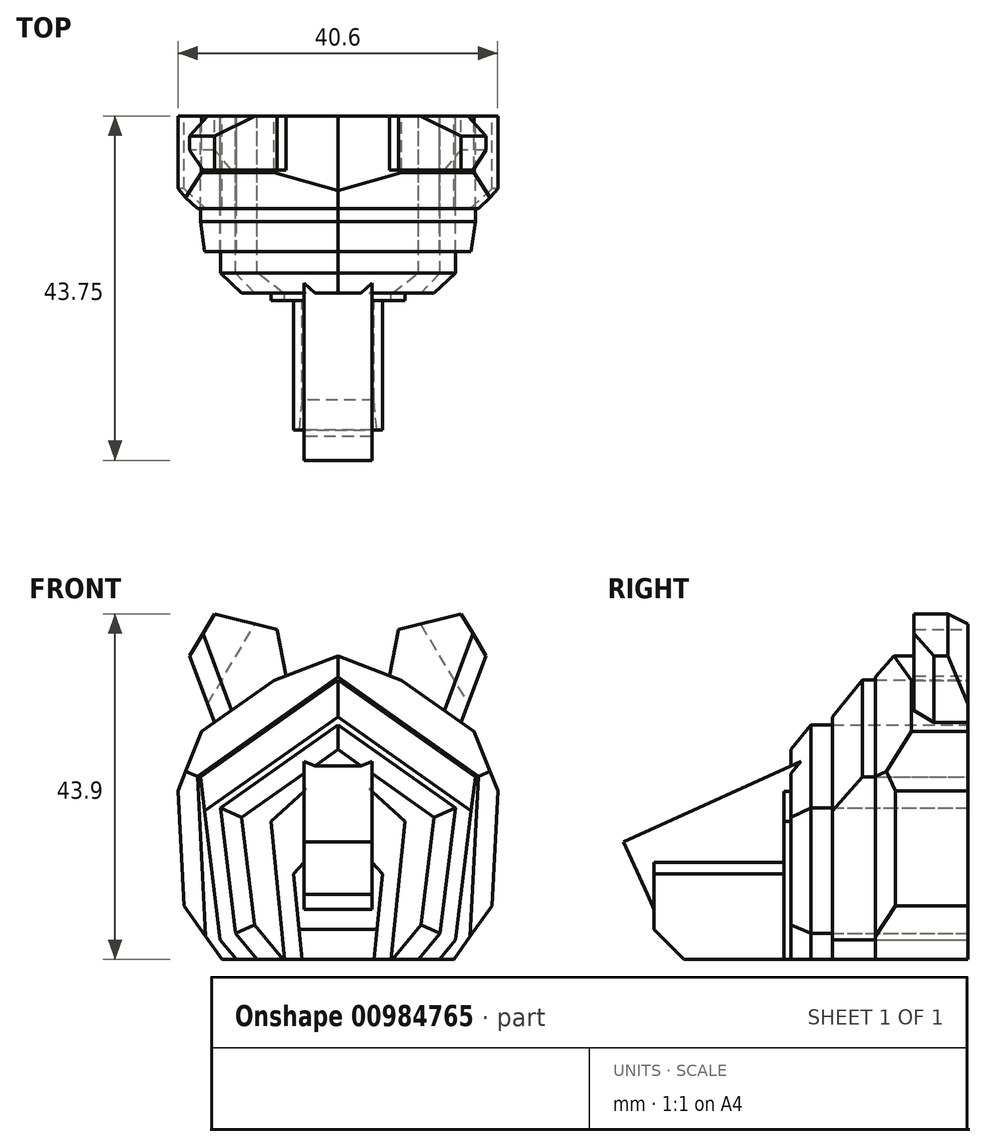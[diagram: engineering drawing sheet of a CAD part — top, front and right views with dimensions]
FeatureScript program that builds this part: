
annotation { "Feature Type Name" : "Feature", "Feature Type Description" : "" }
export const myFeature = defineFeature(function(context is Context, id is Id, definition is map)
    precondition{}
    {
        {
            var Q0;
            Q0=qCreatedBy(makeId("Front.planeOp"),FACE);
            var sketch = newSketch(context, id + "F0", { "sketchPlane" : qUnion([Q0])});
            skLineSegment(sketch, "E0", {"start": v(0, 23) * mm, "end": v(-2.53, 23) * mm});
            skLineSegment(sketch, "E1", {"start": v(-2.53, 23) * mm, "end": v(-8.52, 17.52) * mm});
            skLineSegment(sketch, "E2", {"start": v(-8.52, 17.52) * mm, "end": v(-6.77, 0) * mm});
            skLineSegment(sketch, "E3.MirrorCS", {"start": v(0, 23) * mm, "end": v(2.53, 23) * mm});
            skLineSegment(sketch, "E4.MirrorCS", {"start": v(2.53, 23) * mm, "end": v(8.52, 17.52) * mm});
            skLineSegment(sketch, "E5.MirrorCS", {"start": v(8.52, 17.52) * mm, "end": v(6.77, 0) * mm});
            skLineSegment(sketch, "E6", {"start": v(2.53, 14.3) * mm, "end": v(5.66, 10.9) * mm});
            skLineSegment(sketch, "E7", {"start": v(5.66, 10.9) * mm, "end": v(4.57, 0) * mm});
            skLineSegment(sketch, "E8", {"start": v(2.53, 14.3) * mm, "end": v(0, 14.3) * mm});
            skLineSegment(sketch, "E9.MirrorCS", {"start": v(-2.53, 14.3) * mm, "end": v(0, 14.3) * mm});
            skLineSegment(sketch, "E10.MirrorCS", {"start": v(-2.53, 14.3) * mm, "end": v(-5.66, 10.9) * mm});
            skLineSegment(sketch, "E11.MirrorCS", {"start": v(-5.66, 10.9) * mm, "end": v(-4.57, 0) * mm});
            skLineSegment(sketch, "E12", {"start": v(0, 29.78) * mm, "end": v(-14.93, 19.24) * mm});
            skLineSegment(sketch, "E13", {"start": v(-14.93, 19.24) * mm, "end": v(-13, 3.32) * mm});
            skLineSegment(sketch, "E14", {"start": v(-13, 3.32) * mm, "end": v(-10.24, 0) * mm});
            skLineSegment(sketch, "E15.MirrorCS", {"start": v(0, 29.78) * mm, "end": v(14.93, 19.24) * mm});
            skLineSegment(sketch, "E16.MirrorCS", {"start": v(14.93, 19.24) * mm, "end": v(13, 3.32) * mm});
            skLineSegment(sketch, "E17.MirrorCS", {"start": v(13, 3.32) * mm, "end": v(10.24, 0) * mm});
            skLineSegment(sketch, "E18", {"start": v(0, 38.59) * mm, "end": v(-8.09, 35.46) * mm});
            skLineSegment(sketch, "E19", {"start": v(-8.09, 35.46) * mm, "end": v(-17.3, 28.95) * mm});
            skLineSegment(sketch, "E20", {"start": v(-17.3, 28.95) * mm, "end": v(-20.3, 21.44) * mm});
            skLineSegment(sketch, "E21", {"start": v(-20.3, 21.44) * mm, "end": v(-19.55, 6.83) * mm});
            skLineSegment(sketch, "E22", {"start": v(-19.55, 6.83) * mm, "end": v(-14.72, 0) * mm});
            skLineSegment(sketch, "E23.MirrorCS", {"start": v(0, 38.59) * mm, "end": v(8.09, 35.46) * mm});
            skLineSegment(sketch, "E24.MirrorCS", {"start": v(17.3, 28.95) * mm, "end": v(20.3, 21.44) * mm});
            skLineSegment(sketch, "E25.MirrorCS", {"start": v(8.09, 35.46) * mm, "end": v(17.3, 28.95) * mm});
            skLineSegment(sketch, "E26.MirrorCS", {"start": v(20.3, 21.44) * mm, "end": v(19.55, 6.83) * mm});
            skLineSegment(sketch, "E27.MirrorCS", {"start": v(19.55, 6.83) * mm, "end": v(14.72, 0) * mm});
            skLineSegment(sketch, "E28", {"start": v(-14.72, 0) * mm, "end": v(14.72, 0) * mm});
            skLineSegment(sketch, "E29", {"start": v(6.58, 36.04) * mm, "end": v(7.72, 41.9) * mm});
            skLineSegment(sketch, "E30", {"start": v(7.72, 41.9) * mm, "end": v(15.66, 43.9) * mm});
            skLineSegment(sketch, "E31", {"start": v(15.66, 43.9) * mm, "end": v(18.82, 38.59) * mm});
            skPoint(sketch, "E32.endSnap0", {"position": v(12.7, 32.2) * mm});
            skLineSegment(sketch, "E33", {"start": v(18.82, 38.59) * mm, "end": v(15.66, 30.1) * mm});
            skLineSegment(sketch, "E34.MirrorCS", {"start": v(-6.58, 36.04) * mm, "end": v(-7.72, 41.9) * mm});
            skLineSegment(sketch, "E35.MirrorCS", {"start": v(-7.72, 41.9) * mm, "end": v(-15.66, 43.9) * mm});
            skLineSegment(sketch, "E36.MirrorCS", {"start": v(-15.66, 43.9) * mm, "end": v(-18.82, 38.59) * mm});
            skLineSegment(sketch, "E37.MirrorCS", {"start": v(-18.82, 38.59) * mm, "end": v(-15.66, 30.1) * mm});
            skLineSegment(sketch, "E38", {"start": v(0, 35.5) * mm, "end": v(-17.46, 23.17) * mm});
            skLineSegment(sketch, "E39", {"start": v(-17.46, 23.17) * mm, "end": v(-14.95, 2.47) * mm});
            skLineSegment(sketch, "E40", {"start": v(-14.95, 2.47) * mm, "end": v(-12.9, 0) * mm});
            skLineSegment(sketch, "E41.MirrorCS", {"start": v(0, 35.5) * mm, "end": v(17.46, 23.17) * mm});
            skLineSegment(sketch, "E42.MirrorCS", {"start": v(17.46, 23.17) * mm, "end": v(14.95, 2.47) * mm});
            skLineSegment(sketch, "E43.MirrorCS", {"start": v(14.95, 2.47) * mm, "end": v(12.9, 0) * mm});
            skSolve(sketch);
        }
        {
            var Q0;
            Q0=qCreatedBy(makeId("Right.planeOp"),FACE);
            var sketch = newSketch(context, id + "F1", { "sketchPlane" : qUnion([Q0])});
            skLineSegment(sketch, "E44", {"start": v(0, 38.33) * mm, "end": v(-11.79, 36.33) * mm});
            skLineSegment(sketch, "E45", {"start": v(-11.79, 36.33) * mm, "end": v(-21.78, 29.2) * mm});
            skLineSegment(sketch, "E46", {"start": v(-21.78, 29.2) * mm, "end": v(-24.49, 0) * mm});
            skLineSegment(sketch, "E47", {"start": v(-22.2, 24.73) * mm, "end": v(-43.75, 14.95) * mm});
            skLineSegment(sketch, "E48", {"start": v(-43.75, 14.95) * mm, "end": v(-40.72, 8.26) * mm});
            skLineSegment(sketch, "E49", {"start": v(-22.78, 18.43) * mm, "end": v(-39.87, 13.75) * mm});
            skLineSegment(sketch, "E50", {"start": v(-39.87, 13.75) * mm, "end": v(-40.72, 8.26) * mm});
            skLineSegment(sketch, "E51", {"start": v(-40.72, 8.26) * mm, "end": v(-37.52, 1.02) * mm});
            skLineSegment(sketch, "E52", {"start": v(-37.52, 1.02) * mm, "end": v(-24.49, 0) * mm});
            skLineSegment(sketch, "E53", {"start": v(-24.49, 0) * mm, "end": v(0, 0) * mm});
            skLineSegment(sketch, "E54", {"start": v(0, 38.33) * mm, "end": v(0, 0) * mm});
            skLineSegment(sketch, "E55", {"start": v(-21.78, 29.2) * mm, "end": v(-21.78, 0) * mm});
            skLineSegment(sketch, "E56", {"start": v(-11.79, 36.33) * mm, "end": v(-11.79, 0) * mm});
            skPoint(sketch, "E56.endSnap0", {"position": v(-12.24, 0) * mm});
            skLineSegment(sketch, "E57", {"start": v(-21.78, 15.58) * mm, "end": v(-11.79, 15.58) * mm});
            skSolve(sketch);
        }
        {
            var Q0;
            Q0=makeQuery(id+"F0.imprint","IMPRINT",FACE,{"disambiguationData":[TD([[makeQuery(id+"F0.imprint","IMPRINT",EDGE,{"derivedFrom":sQuery(id+"F0.wireOp",EDGE,"E6")}),-1.0]])]});
            var Q1;
            Q1=sQuery(id+"F1.wireOp",VERTEX,"E49.end");
            extrude(context, id + "F2", {"entities" : qUnion([Q0]), "endBound" : BoundingType.UP_TO_VERTEX, "depth" : 25.4 * mm, "endBoundEntityVertex" : qUnion([Q1]), "offsetDistance" : 25.4 * mm});
        }
        {
            var Q0;
            Q0=makeQuery(id+"F0.imprint","IMPRINT",FACE,{"disambiguationData":[TD([[makeQuery(id+"F0.imprint","IMPRINT",EDGE,{"derivedFrom":sQuery(id+"F0.wireOp",EDGE,"E0")}),1.0]])]});
            extrude(context, id + "F3", {"entities" : qUnion([Q0]), "operationType" : NewBodyOperationType.ADD, "depth" : 23.42 * mm, "offsetDistance" : 25.4 * mm});
        }
        {
            var Q0;
            {var subQ0=sQuery(id+"F1.wireOp",EDGE,"E49");Q0=makeQuery(id+"F1.imprint","IMPRINT",FACE,{"disambiguationData":[TD([[makeQuery(id+"F1.imprint","IMPRINT",EDGE,{"derivedFrom":subQ0}),1.0]])]});}
            var Q1;
            Q1=makeQuery(id+"F3.opExtrude","CAP_VERTEX",VERTEX,{"disambiguationData":[OSD([sQuery(id+"F0.wireOp",EDGE,"E6"),sQuery(id+"F0.wireOp",EDGE,"E8"),sQuery(id+"F0.wireOp",EDGE,"E9.MirrorCS")])],"isStart":false});
            extrude(context, id + "F4", {"entities" : qUnion([Q0]), "operationType" : NewBodyOperationType.ADD, "endBound" : BoundingType.UP_TO_VERTEX, "depth" : 25.4 * mm, "endBoundEntityVertex" : qUnion([Q1]), "offsetDistance" : 25.4 * mm});
        }
        {
            var Q0;
            {var subQ0=sQuery(id+"F1.wireOp",EDGE,"E49");Q0=makeQuery(id+"F1.imprint","IMPRINT",FACE,{"disambiguationData":[TD([[makeQuery(id+"F1.imprint","IMPRINT",EDGE,{"derivedFrom":subQ0}),1.0]])]});}
            var Q1;
            Q1=makeQuery(id+"F3.opExtrude","CAP_VERTEX",VERTEX,{"disambiguationData":[OSD([sQuery(id+"F0.wireOp",EDGE,"E8"),sQuery(id+"F0.wireOp",EDGE,"E9.MirrorCS"),sQuery(id+"F0.wireOp",EDGE,"E10.MirrorCS")])],"isStart":false});
            extrude(context, id + "F5", {"entities" : qUnion([Q0]), "operationType" : NewBodyOperationType.ADD, "endBound" : BoundingType.UP_TO_VERTEX, "oppositeDirection" : true, "depth" : 25.4 * mm, "endBoundEntityVertex" : qUnion([Q1]), "offsetDistance" : 25.4 * mm});
        }
        {
            var Q0;
            {var subQ1=sQuery(id+"F1.wireOp",EDGE,"E47");Q0=makeQuery(id+"F1.imprint","IMPRINT",FACE,{"disambiguationData":[TD([[makeQuery(id+"F1.imprint","IMPRINT",EDGE,{"derivedFrom":subQ1}),1.0]])]});}
            var Q1;
            Q1=makeQuery(id+"F2.opExtrude","CAP_VERTEX",VERTEX,{"disambiguationData":[OSD([sQuery(id+"F0.wireOp",EDGE,"E6"),sQuery(id+"F0.wireOp",EDGE,"E8"),sQuery(id+"F0.wireOp",EDGE,"E9.MirrorCS")])],"isStart":false});
            extrude(context, id + "F6", {"entities" : qUnion([Q0]), "operationType" : NewBodyOperationType.ADD, "depth" : 4.32 * mm, "endBoundEntityVertex" : qUnion([Q1]), "offsetDistance" : 25.4 * mm});
        }
        {
            var Q0;
            {var subQ1=sQuery(id+"F1.wireOp",EDGE,"E47");Q0=makeQuery(id+"F1.imprint","IMPRINT",FACE,{"disambiguationData":[TD([[makeQuery(id+"F1.imprint","IMPRINT",EDGE,{"derivedFrom":subQ1}),1.0]])]});}
            var Q1;
            Q1=makeQuery(id+"F2.opExtrude","CAP_VERTEX",VERTEX,{"disambiguationData":[OSD([sQuery(id+"F0.wireOp",EDGE,"E8"),sQuery(id+"F0.wireOp",EDGE,"E9.MirrorCS"),sQuery(id+"F0.wireOp",EDGE,"E10.MirrorCS")])],"isStart":false});
            extrude(context, id + "F7", {"entities" : qUnion([Q0]), "operationType" : NewBodyOperationType.ADD, "oppositeDirection" : true, "depth" : 4.32 * mm, "endBoundEntityVertex" : qUnion([Q1]), "offsetDistance" : 25.4 * mm});
        }
        {
            var Q0;
            {var subQ0=sQuery(id+"F1.wireOp",EDGE,"E49");Q0=makeQuery(id+"F1.imprint","IMPRINT",FACE,{"disambiguationData":[TD([[makeQuery(id+"F1.imprint","IMPRINT",EDGE,{"derivedFrom":subQ0}),1.0]])]});}
            extrude(context, id + "F8", {"entities" : qUnion([Q0]), "operationType" : NewBodyOperationType.ADD, "depth" : 4.32 * mm, "offsetDistance" : 25.4 * mm});
        }
        {
            var Q0;
            {var subQ0=sQuery(id+"F1.wireOp",EDGE,"E49");Q0=makeQuery(id+"F1.imprint","IMPRINT",FACE,{"disambiguationData":[TD([[makeQuery(id+"F1.imprint","IMPRINT",EDGE,{"derivedFrom":subQ0}),1.0]])]});}
            extrude(context, id + "F9", {"entities" : qUnion([Q0]), "operationType" : NewBodyOperationType.ADD, "depth" : -4.32 * mm, "offsetDistance" : 25.4 * mm});
        }
        {
            var Q0;
            Q0=makeQuery(id+"F0.imprint","IMPRINT",FACE,{"disambiguationData":[TD([[makeQuery(id+"F0.imprint","IMPRINT",EDGE,{"derivedFrom":sQuery(id+"F0.wireOp",EDGE,"E0")}),-1.0]])]});
            extrude(context, id + "F10", {"entities" : qUnion([Q0]), "operationType" : NewBodyOperationType.ADD, "depth" : 22.48 * mm, "offsetDistance" : 25.4 * mm});
        }
        {
            var Q0;
            {var subQ0=sQuery(id+"F0.wireOp",EDGE,"E34.MirrorCS");Q0=makeQuery(id+"F0.imprint","IMPRINT",FACE,{"disambiguationData":[TD([[makeQuery(id+"F0.imprint","IMPRINT",EDGE,{"derivedFrom":subQ0}),1.0]])]});}
            extrude(context, id + "F11", {"entities" : qUnion([Q0]), "operationType" : NewBodyOperationType.ADD, "depth" : 6.86 * mm, "offsetDistance" : 25.4 * mm});
        }
        {
            var Q0;
            {var subQ0=sQuery(id+"F0.wireOp",EDGE,"E29");Q0=makeQuery(id+"F0.imprint","IMPRINT",FACE,{"disambiguationData":[TD([[makeQuery(id+"F0.imprint","IMPRINT",EDGE,{"derivedFrom":subQ0}),-1.0]])]});}
            extrude(context, id + "F12", {"entities" : qUnion([Q0]), "operationType" : NewBodyOperationType.ADD, "depth" : 6.86 * mm, "offsetDistance" : 25.4 * mm});
        }
        {
            var Q0;
            Q0=makeQuery(id+"F2.opExtrude","CAP_EDGE",EDGE,{"disambiguationData":[OSD([sQuery(id+"F0.wireOp",EDGE,"E28")])],"isStart":false});
            chamfer(context, id + "F13", {"entities" : qUnion([Q0]), "width" : 3.8 * mm, "tangentPropagation" : true});
        }
        {
            var Q0;
            {var subQ8=sQuery(id+"F0.wireOp",EDGE,"E20");Q0=makeQuery(id+"F0.imprint","IMPRINT",FACE,{"disambiguationData":[TD([[makeQuery(id+"F0.imprint","IMPRINT",EDGE,{"derivedFrom":subQ8}),1.0]])]});}
            var Q1;
            Q1=sQuery(id+"F1.wireOp",VERTEX,"E44.end");
            extrude(context, id + "F14", {"entities" : qUnion([Q0]), "endBound" : BoundingType.UP_TO_VERTEX, "depth" : 25.4 * mm, "endBoundEntityVertex" : qUnion([Q1]), "offsetDistance" : 25.4 * mm});
        }
        {
            var Q0;
            Q0=makeQuery(id+"F10.opExtrude","CAP_EDGE",EDGE,{"disambiguationData":[OSD([sQuery(id+"F0.wireOp",EDGE,"E12")])],"isStart":false});
            var Q1;
            Q1=makeQuery(id+"F10.opExtrude","CAP_EDGE",EDGE,{"disambiguationData":[OSD([sQuery(id+"F0.wireOp",EDGE,"E15.MirrorCS")])],"isStart":false});
            chamfer(context, id + "F15", {"entities" : qUnion([Q0, Q1]), "width" : 2.54 * mm, "tangentPropagation" : true});
        }
        {
            var Q0;
            Q0=makeQuery(id+"F10.opExtrude","CAP_EDGE",EDGE,{"disambiguationData":[OSD([sQuery(id+"F0.wireOp",EDGE,"E14")])],"isStart":false});
            var Q1;
            Q1=makeQuery(id+"F10.opExtrude","CAP_EDGE",EDGE,{"disambiguationData":[OSD([sQuery(id+"F0.wireOp",EDGE,"E17.MirrorCS")])],"isStart":false});
            chamfer(context, id + "F16", {"entities" : qUnion([Q0, Q1]), "width" : 2.54 * mm, "tangentPropagation" : true});
        }
        {
            var Q0;
            Q0=makeQuery(id+"F14.opExtrude","CAP_EDGE",EDGE,{"disambiguationData":[OSD([sQuery(id+"F0.wireOp",EDGE,"E19")])],"isStart":false});
            var Q1;
            Q1=makeQuery(id+"F14.opExtrude","CAP_EDGE",EDGE,{"disambiguationData":[OSD([sQuery(id+"F0.wireOp",EDGE,"E25.MirrorCS")])],"isStart":false});
            chamfer(context, id + "F17", {"entities" : qUnion([Q0, Q1]), "chamferType" : ChamferType.TWO_OFFSETS, "width1" : 4.32 * mm, "oppositeDirection" : false, "width2" : 4.57 * mm, "tangentPropagation" : true});
        }
        {
            var Q0;
            Q0=makeQuery(id+"F11.opExtrude","CAP_EDGE",EDGE,{"disambiguationData":[OSD([sQuery(id+"F0.wireOp",EDGE,"E36.MirrorCS")])],"isStart":true});
            chamfer(context, id + "F18", {"entities" : qUnion([Q0]), "chamferType" : ChamferType.TWO_OFFSETS, "width1" : 2.54 * mm, "oppositeDirection" : false, "width2" : 5.08 * mm, "tangentPropagation" : true});
        }
        {
            var Q0;
            Q0=makeQuery(id+"F12.opExtrude","CAP_EDGE",EDGE,{"disambiguationData":[OSD([sQuery(id+"F0.wireOp",EDGE,"E31")])],"isStart":true});
            chamfer(context, id + "F19", {"entities" : qUnion([Q0]), "chamferType" : ChamferType.TWO_OFFSETS, "width1" : 5.08 * mm, "oppositeDirection" : false, "width2" : 2.54 * mm, "tangentPropagation" : true});
        }
        {
            var Q0;
            Q0=makeQuery(id+"F11.opExtrude","CAP_EDGE",EDGE,{"disambiguationData":[OSD([sQuery(id+"F0.wireOp",EDGE,"E37.MirrorCS")])],"isStart":false});
            var Q1;
            Q1=makeQuery(id+"F12.opExtrude","CAP_EDGE",EDGE,{"disambiguationData":[OSD([sQuery(id+"F0.wireOp",EDGE,"E33")])],"isStart":false});
            chamfer(context, id + "F20", {"entities" : qUnion([Q0, Q1]), "width" : 2.54 * mm, "tangentPropagation" : true});
        }
        {
            var Q0;
            Q0=makeQuery(id+"F14.opExtrude","CAP_EDGE",EDGE,{"disambiguationData":[OSD([sQuery(id+"F0.wireOp",EDGE,"E21")])],"isStart":false});
            var Q1;
            Q1=makeQuery(id+"F14.opExtrude","CAP_EDGE",EDGE,{"disambiguationData":[OSD([sQuery(id+"F0.wireOp",EDGE,"E26.MirrorCS")])],"isStart":false});
            chamfer(context, id + "F21", {"entities" : qUnion([Q0, Q1]), "width" : 2.54 * mm, "tangentPropagation" : true});
        }
        {
            var Q0;
            Q0=makeQuery(id+"F10.opExtrude","CAP_EDGE",EDGE,{"disambiguationData":[OSD([sQuery(id+"F0.wireOp",EDGE,"E13")])],"isStart":false});
            var Q1;
            Q1=makeQuery(id+"F10.opExtrude","CAP_EDGE",EDGE,{"disambiguationData":[OSD([sQuery(id+"F0.wireOp",EDGE,"E16.MirrorCS")])],"isStart":false});
            chamfer(context, id + "F22", {"entities" : qUnion([Q0, Q1]), "width" : 2.54 * mm, "tangentPropagation" : true});
        }
        {
            var Q0;
            Q0=makeQuery(id+"F0.imprint","IMPRINT",FACE,{"disambiguationData":[TD([[makeQuery(id+"F0.imprint","IMPRINT",EDGE,{"derivedFrom":sQuery(id+"F0.wireOp",EDGE,"E12")}),-1.0]])]});
            extrude(context, id + "F23", {"entities" : qUnion([Q0]), "depth" : 17.25 * mm, "offsetDistance" : 25.4 * mm});
        }
        {
            var Q0;
            Q0=makeQuery(id+"F23.opExtrude","CAP_EDGE",EDGE,{"disambiguationData":[OSD([sQuery(id+"F0.wireOp",EDGE,"E38")])],"isStart":false});
            var Q1;
            Q1=makeQuery(id+"F23.opExtrude","CAP_EDGE",EDGE,{"disambiguationData":[OSD([sQuery(id+"F0.wireOp",EDGE,"E41.MirrorCS")])],"isStart":false});
            chamfer(context, id + "F24", {"entities" : qUnion([Q0, Q1]), "width" : 3.8 * mm, "tangentPropagation" : true});
        }
    });
